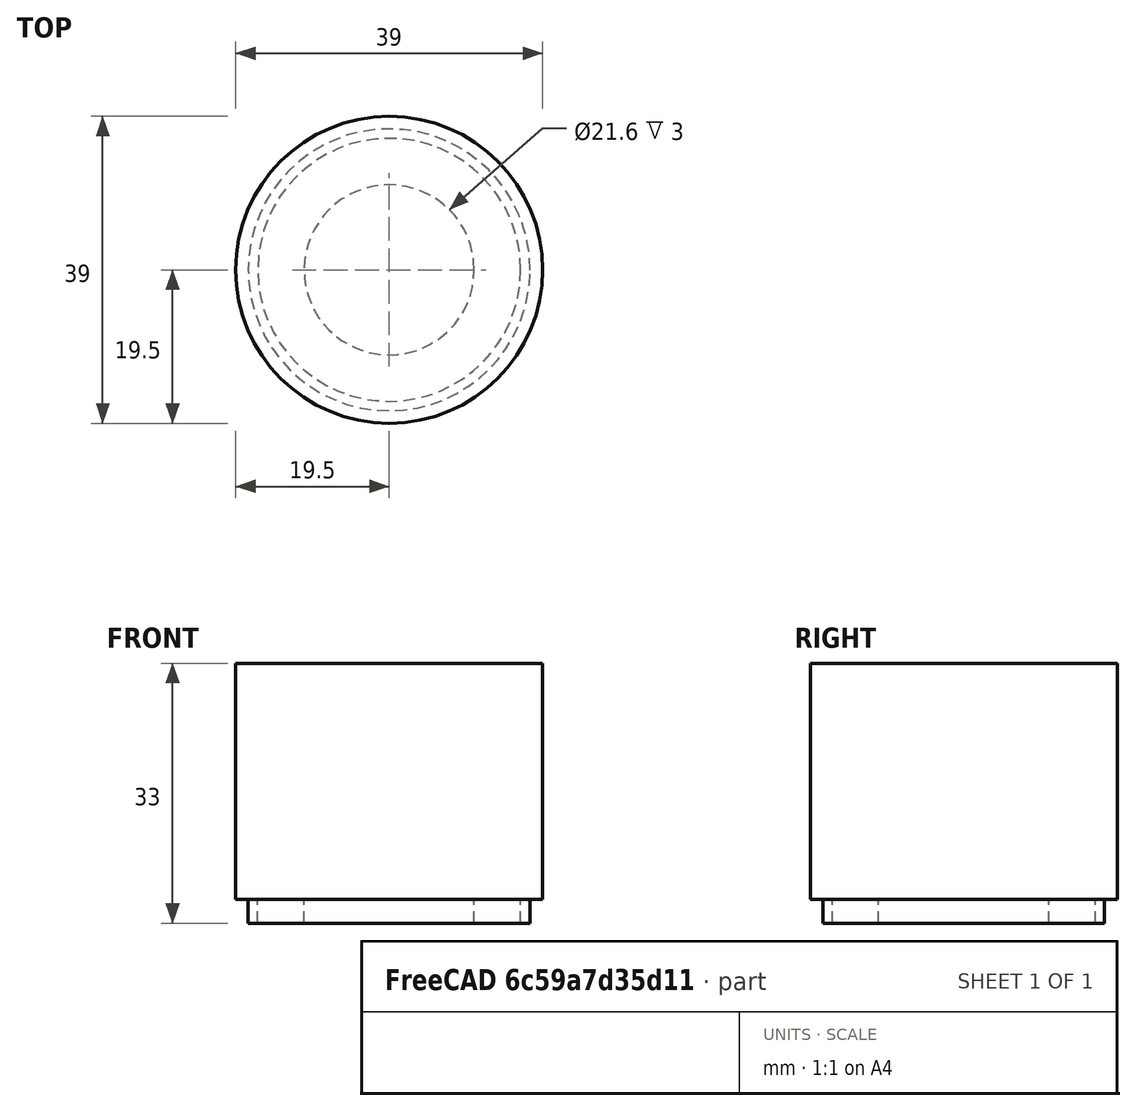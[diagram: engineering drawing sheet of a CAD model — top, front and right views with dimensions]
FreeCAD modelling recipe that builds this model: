
FCSTD DOCUMENT  (FreeCAD 0.19R24276 (Git))
Label: alarga_soporte
License: All rights reserved
LicenseURL: http://en.wikipedia.org/wiki/All_rights_reserved
objects: Part::Cylinder×5, Part::MultiFuse×2, Mesh::Feature×2, Part::Feature×1, Part::Cut×1
note: 9 computed .brp shape members not serialized (recipe doc carries the construction recipe); baked Part::Feature solids carry a one-line shape summary decoded from their .brp

FEATURE [Part::Feature] fat_mounting001001
  shape: bbox 58.9 x 69 x 60 mm, 1434 faces, 0 solids (baked)
FEATURE [Part::Cylinder] Cylinder
  Angle = 360
  AttacherType = Attacher::AttachEngine3D
  Height = 3
  Placement = pos=(0,0,57) rot=(0,0,1;0rad)
  Radius = 10.3
FEATURE [Part::Cylinder] Cylinder001
  Angle = 360
  AttacherType = Attacher::AttachEngine3D
  Height = 30
  Placement = pos=(0,0,60) rot=(0,0,1;0rad)
  Radius = 19.5
FEATURE [Part::MultiFuse] Fusion
  Refine = true
  Shapes = -> [Cylinder,Cylinder001]
FEATURE [Part::Cylinder] Cylinder002
  Angle = 360
  AttacherType = Attacher::AttachEngine3D
  Height = 3
  Placement = pos=(0,0,57) rot=(0,0,1;0rad)
  Radius = 10.8
FEATURE [Part::Cylinder] Cylinder003
  Angle = 360
  AttacherType = Attacher::AttachEngine3D
  Height = 3
  Placement = pos=(0,0,57) rot=(0,0,1;0rad)
  Radius = 17.9
FEATURE [Part::MultiFuse] Fusion001  label="alargador"
  Refine = true
  Shapes = -> [Cylinder003,Fusion]
FEATURE [Part::Cylinder] Cylinder004
  Angle = 360
  AttacherType = Attacher::AttachEngine3D
  Height = 3
  Placement = pos=(0,0,57) rot=(0,0,1;0rad)
  Radius = 16.7
FEATURE [Part::Cut] Cut  label="anillo"
  Base = -> Cylinder004
  Refine = true
  Tool = -> Cylinder002
FEATURE [Mesh::Feature] Mesh  label="alargador (Meshed)"
FEATURE [Mesh::Feature] Mesh001  label="anillo (Meshed)"
